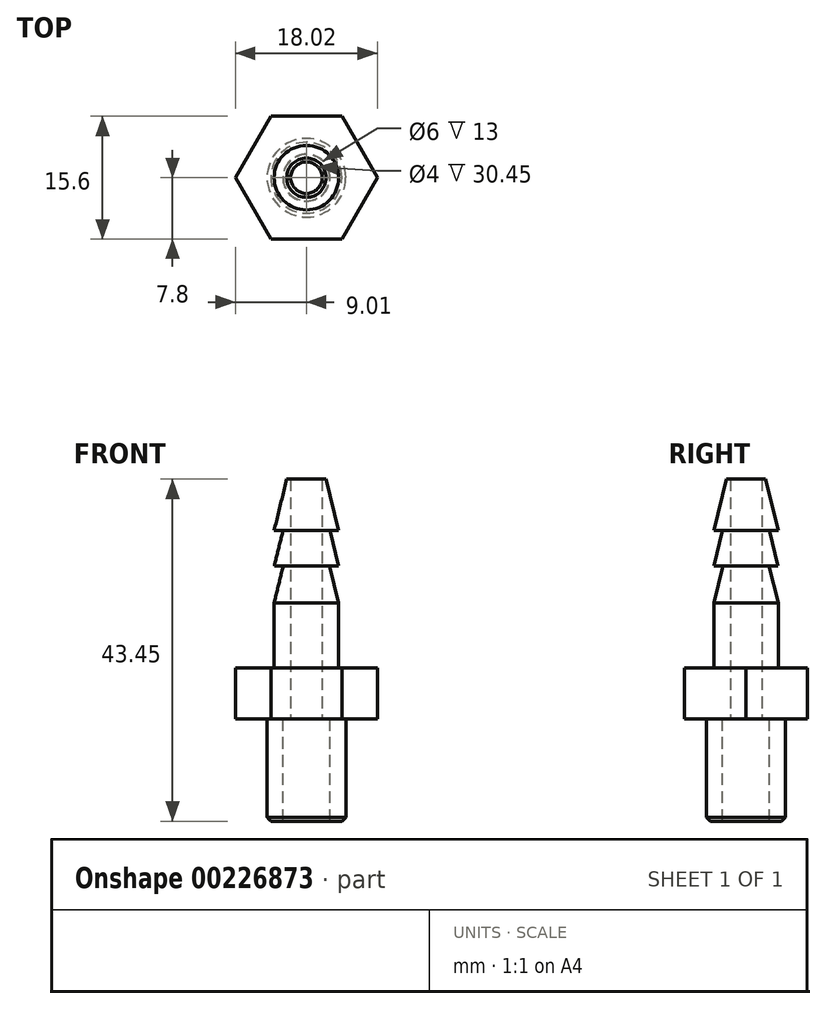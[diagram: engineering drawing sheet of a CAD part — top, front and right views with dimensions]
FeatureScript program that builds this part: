
annotation { "Feature Type Name" : "Feature", "Feature Type Description" : "" }
export const myFeature = defineFeature(function(context is Context, id is Id, definition is map)
    precondition{}
    {
        {
            var Q0;
            Q0=qCreatedBy(makeId("Top.planeOp"),FACE);
            var sketch = newSketch(context, id + "F0", { "sketchPlane" : qUnion([Q0])});
            skCircle(sketch, "E0.cCircle", {"center": v(0, 0) * mm, "radius": 7.8 * mm, "construction": true});
            skLineSegment(sketch, "E0.0", {"start": v(9, 0) * mm, "end": v(4.5, -7.8) * mm});
            skLineSegment(sketch, "E0.1", {"start": v(4.5, -7.8) * mm, "end": v(-4.5, -7.8) * mm});
            skLineSegment(sketch, "E0.2", {"start": v(-4.5, -7.8) * mm, "end": v(-9, 0) * mm});
            skLineSegment(sketch, "E0.3", {"start": v(-9, 0) * mm, "end": v(-4.5, 7.8) * mm});
            skLineSegment(sketch, "E0.4", {"start": v(-4.5, 7.8) * mm, "end": v(4.5, 7.8) * mm});
            skLineSegment(sketch, "E0.5", {"start": v(4.5, 7.8) * mm, "end": v(9, 0) * mm});
            skPoint(sketch, "E0.0.midPoint", {"position": v(6.75, -3.9) * mm});
            skSolve(sketch);
        }
        {
            var Q0;
            Q0=makeQuery(id+"F0.imprint","IMPRINT",FACE,{"disambiguationData":[TD([[makeQuery(id+"F0.imprint","IMPRINT",EDGE,{"derivedFrom":sQuery(id+"F0.wireOp",EDGE,"E0.0")}),-1.0]])]});
            extrude(context, id + "F1", {"entities" : qUnion([Q0]), "depth" : 6.45 * mm});
        }
        {
            var Q0;
            Q0=makeQuery(id+"F1.opExtrude","CAP_FACE",FACE,{"disambiguationData":[OSD([sQuery(id+"F0.wireOp",EDGE,"E0.0"),sQuery(id+"F0.wireOp",EDGE,"E0.1"),sQuery(id+"F0.wireOp",EDGE,"E0.2"),sQuery(id+"F0.wireOp",EDGE,"E0.3"),sQuery(id+"F0.wireOp",EDGE,"E0.4"),sQuery(id+"F0.wireOp",EDGE,"E0.5")])],"isStart":true});
            var sketch = newSketch(context, id + "F2", { "sketchPlane" : qUnion([Q0])});
            skCircle(sketch, "E1", {"center": v(0, 0) * mm, "radius": 5 * mm});
            skCircle(sketch, "E2", {"center": v(0, 0) * mm, "radius": 3 * mm});
            skSolve(sketch);
        }
        {
            var Q0;
            Q0=makeQuery(id+"F2.imprint","IMPRINT",FACE,{"disambiguationData":[TD([[makeQuery(id+"F2.imprint","IMPRINT",EDGE,{"derivedFrom":sQuery(id+"F2.wireOp",EDGE,"E1")}),1.0]])]});
            extrude(context, id + "F3", {"entities" : qUnion([Q0]), "operationType" : NewBodyOperationType.ADD, "depth" : 13 * mm});
        }
        {
            var Q0;
            Q0=makeQuery(id+"F3.opExtrude","CAP_EDGE",EDGE,{"disambiguationData":[OSD([sQuery(id+"F2.wireOp",EDGE,"E1")])],"isStart":false});
            chamfer(context, id + "F4", {"entities" : qUnion([Q0]), "width" : .5 * mm, "tangentPropagation" : true});
        }
        {
            var Q0;
            Q0=qCreatedBy(makeId("Front.planeOp"),FACE);
            var sketch = newSketch(context, id + "F5", { "sketchPlane" : qUnion([Q0])});
            skLineSegment(sketch, "E3.bottom", {"start": v(-2, 30.45) * mm, "end": v(-2.5, 30.45) * mm});
            skLineSegment(sketch, "E3.top", {"start": v(-2, 6.45) * mm, "end": v(-4.1, 6.45) * mm});
            skLineSegment(sketch, "E4", {"start": v(-2, 30.45) * mm, "end": v(-2, 6.45) * mm});
            skLineSegment(sketch, "E5", {"start": v(-2.5, 30.45) * mm, "end": v(-4.1, 23.95) * mm});
            skLineSegment(sketch, "E6", {"start": v(-4.1, 23.95) * mm, "end": v(-2.97, 23.95) * mm});
            skLineSegment(sketch, "E7", {"start": v(-4.1, 19.45) * mm, "end": v(-2.94, 19.45) * mm});
            skLineSegment(sketch, "E8.trimOffspring", {"start": v(-4.1, 19.45) * mm, "end": v(-4.1, 19.35) * mm});
            skLineSegment(sketch, "E9.0.1.0", {"start": v(-2.97, 23.95) * mm, "end": v(-4.1, 19.35) * mm});
            skLineSegment(sketch, "E9.0.2.0", {"start": v(-2.94, 19.45) * mm, "end": v(-4.1, 14.75) * mm});
            skLineSegment(sketch, "E9.direction1", {"start": v(-4.1, 23.95) * mm, "end": v(-2.97, 23.95) * mm, "construction": true});
            skLineSegment(sketch, "E9.direction2", {"start": v(-4.1, 23.95) * mm, "end": v(-4.1, 19.35) * mm, "construction": true});
            skPoint(sketch, "E10.orphan", {"position": v(-2.5, 25.85) * mm});
            skLineSegment(sketch, "E11.trimOffspring", {"start": v(-2.53, 23.95) * mm, "end": v(20.9, 23.95) * mm, "construction": true});
            skPoint(sketch, "E12.orphan", {"position": v(-2.5, 21.25) * mm});
            skLineSegment(sketch, "E13.trimOffspring", {"start": v(-4.1, 14.75) * mm, "end": v(-4.1, 6.45) * mm});
            skLineSegment(sketch, "E14", {"start": v(0, 0) * mm, "end": v(0, 35.28) * mm, "construction": true});
            skSolve(sketch);
        }
        {
            var Q0;
            Q0 = qSketchRegion(id + "F5", true);
            var Q1;
            Q1=sQuery(id+"F5.wireOp",EDGE,"E14");
            revolve(context, id + "F6", {"operationType" : NewBodyOperationType.ADD, "entities" : qUnion([Q0]), "axis" : qUnion([Q1]), "revolveType" : RevolveType.FULL});
        }
        {
            var Q0;
            {var subQ0=sQuery(id+"F0.wireOp",EDGE,"E0.3");var subQ1=sQuery(id+"F0.wireOp",EDGE,"E0.2");var subQ2=sQuery(id+"F0.wireOp",EDGE,"E0.1");var subQ3=sQuery(id+"F0.wireOp",EDGE,"E0.0");var subQ4=sQuery(id+"F0.wireOp",EDGE,"E0.4");var subQ5=sQuery(id+"F0.wireOp",EDGE,"E0.5");Q0=makeQuery(id+"F6.boolean.opBoolean","SPLIT",FACE,{"disambiguationData":[TD([makeQuery(id+"F1.opExtrude","SWEPT_FACE",FACE,{"disambiguationData":[OSD([subQ3])]})])],"derivedFrom":makeQuery(id+"F1.opExtrude","CAP_FACE",FACE,{"disambiguationData":[OSD([subQ3,subQ2,subQ1,subQ0,subQ4,subQ5])],"isStart":false})});}
            var sketch = newSketch(context, id + "F7", { "sketchPlane" : qUnion([Q0])});
            skCircle(sketch, "E15", {"center": v(0, 0) * mm, "radius": 2 * mm});
            skSolve(sketch);
        }
        {
            var Q0;
            Q0 = qSketchRegion(id + "F7", true);
            extrude(context, id + "F8", {"entities" : qUnion([Q0]), "operationType" : NewBodyOperationType.REMOVE, "oppositeDirection" : true, "depth" : 75 * mm});
        }
        {
            var Q0;
            {var subQ0=sQuery(id+"F5.wireOp",EDGE,"E9.0.1.0");var subQ1=sQuery(id+"F5.wireOp",EDGE,"E7");Q0=makeQuery(id+"F6.boolean.opBoolean","MERGE",BODY,{"derivedFrom":[makeQuery(id+"F6.opRevolve","SWEPT_BODY",BODY,{"disambiguationData":[OSD([sQuery(id+"F5.wireOp",EDGE,"E3.bottom"),sQuery(id+"F5.wireOp",EDGE,"E3.top"),sQuery(id+"F5.wireOp",EDGE,"E4"),sQuery(id+"F5.wireOp",EDGE,"E5"),sQuery(id+"F5.wireOp",EDGE,"E6"),subQ1,subQ0,sQuery(id+"F5.wireOp",EDGE,"E9.0.2.0"),sQuery(id+"F5.wireOp",EDGE,"E13.trimOffspring")])]}),makeQuery(id+"F6.opRevolve","SWEPT_BODY",BODY,{"disambiguationData":[OSD([subQ1,sQuery(id+"F5.wireOp",EDGE,"E8.trimOffspring"),subQ0])]})]});}
            deleteBodies(context, id + "F9", {"entities" : qUnion([Q0])});
        }
    });
